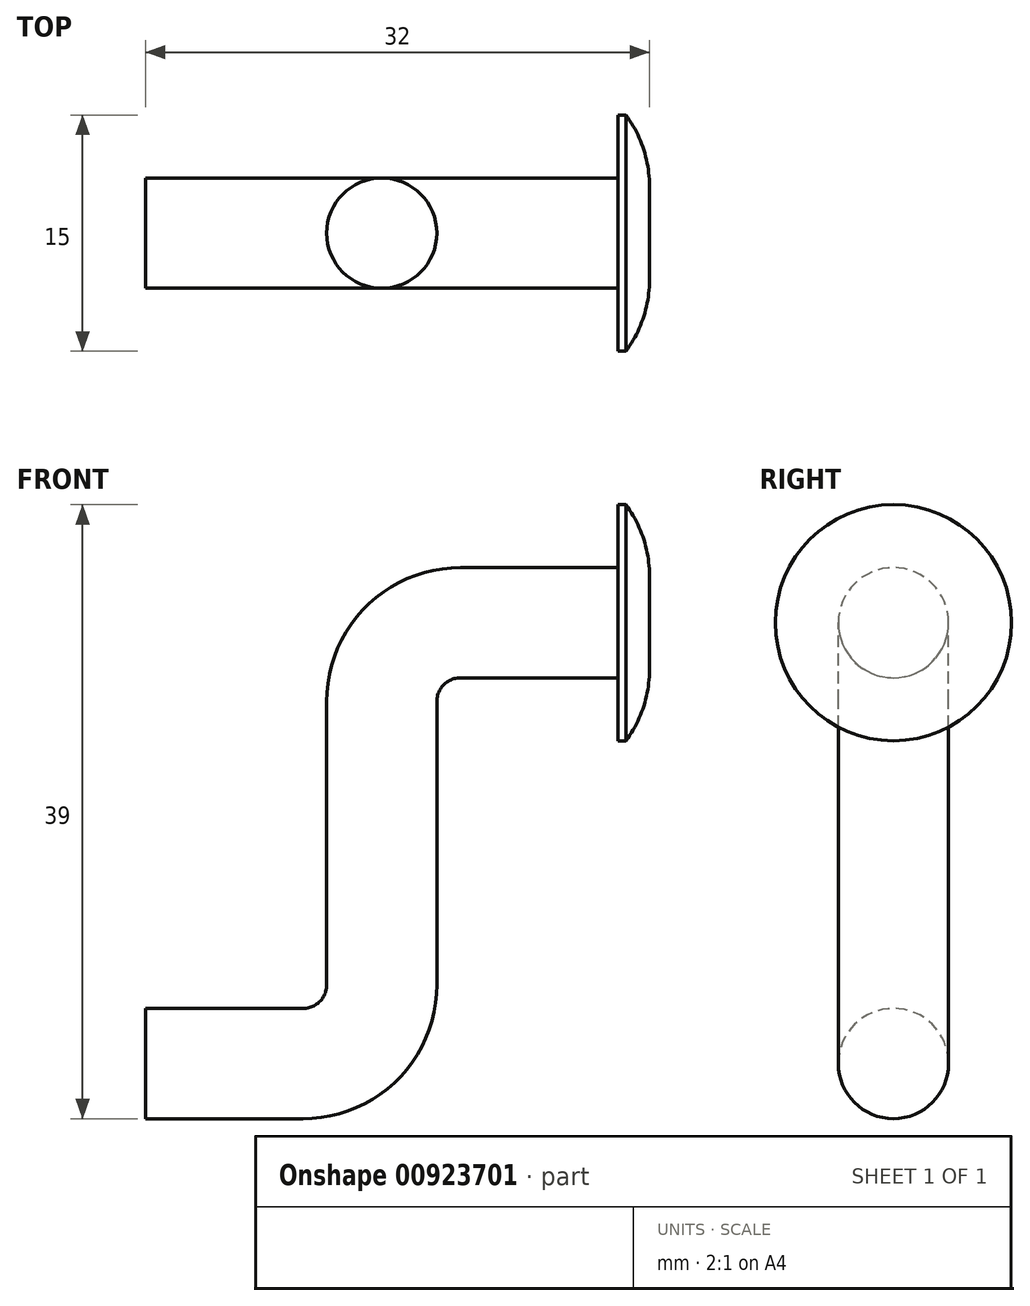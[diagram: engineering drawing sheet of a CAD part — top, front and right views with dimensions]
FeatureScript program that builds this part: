
annotation { "Feature Type Name" : "Feature", "Feature Type Description" : "" }
export const myFeature = defineFeature(function(context is Context, id is Id, definition is map)
    precondition{}
    {
        {
            var Q0;
            Q0=qCreatedBy(makeId("Front.planeOp"),FACE);
            var sketch = newSketch(context, id + "F0", { "sketchPlane" : qUnion([Q0])});
            skLineSegment(sketch, "E0", {"start": v(0, 0) * mm, "end": v(10, 0) * mm});
            skLineSegment(sketch, "E1", {"start": v(15, 5) * mm, "end": v(15, 23) * mm});
            skLineSegment(sketch, "E2", {"start": v(20, 28) * mm, "end": v(30, 28) * mm});
            skPoint(sketch, "E3.visualSharp", {"position": v(15, 0) * mm});
            skArc(sketch, "E3.filletArc", {"start": v(10, 0) * mm, "mid": v(13.54, 1.46) * mm, "end": v(15, 5) * mm});
            skPoint(sketch, "E4.visualSharp", {"position": v(15, 28) * mm});
            skArc(sketch, "E4.filletArc", {"start": v(20, 28) * mm, "mid": v(16.46, 26.54) * mm, "end": v(15, 23) * mm});
            skSolve(sketch);
        }
        {
            var Q0;
            Q0=qCreatedBy(makeId("Right.planeOp"),FACE);
            var sketch = newSketch(context, id + "F1", { "sketchPlane" : qUnion([Q0])});
            skCircle(sketch, "E5", {"center": v(0, 0) * mm, "radius": 3.5 * mm});
            skSolve(sketch);
        }
        {
            var Q0;
            Q0=makeQuery(id+"F1.imprint","IMPRINT",FACE,{"disambiguationData":[TD([[makeQuery(id+"F1.imprint","IMPRINT",EDGE,{"derivedFrom":sQuery(id+"F1.wireOp",EDGE,"E5")}),1.0]])]});
            var Q1;
            Q1=sQuery(id+"F0.wireOp",EDGE,"E0");
            var Q2;
            Q2=sQuery(id+"F0.wireOp",EDGE,"E3.filletArc");
            var Q3;
            Q3=sQuery(id+"F0.wireOp",EDGE,"E1");
            var Q4;
            Q4=sQuery(id+"F0.wireOp",EDGE,"E4.filletArc");
            var Q5;
            Q5=sQuery(id+"F0.wireOp",EDGE,"E2");
            sweep(context, id + "F2", {"profiles" : qUnion([Q0]), "path" : qUnion([Q1, Q2, Q3, Q4, Q5])});
        }
        {
            var Q0;
            Q0=makeQuery(id+"F2.opSweep","CAP_FACE",FACE,{"disambiguationData":[OSD([sQuery(id+"F0.wireOp",VERTEX,"E2.end"),sQuery(id+"F1.wireOp",EDGE,"E5")])],"isStart":false});
            var sketch = newSketch(context, id + "F3", { "sketchPlane" : qUnion([Q0])});
            skCircle(sketch, "E6", {"center": v(0, 28) * mm, "radius": 7.5 * mm});
            skSolve(sketch);
        }
        {
            var Q0;
            Q0=makeQuery(id+"F3.imprint","IMPRINT",FACE,{"disambiguationData":[TD([[makeQuery(id+"F3.imprint","IMPRINT",EDGE,{"derivedFrom":sQuery(id+"F3.wireOp",EDGE,"E6")}),1.0]])]});
            extrude(context, id + "F4", {"entities" : qUnion([Q0]), "depth" : 0.5 * mm, "offsetDistance" : 25 * mm});
        }
        {
            var Q0;
            Q0=makeQuery(id+"F2.opSweep","CAP_FACE",FACE,{"disambiguationData":[OSD([sQuery(id+"F0.wireOp",VERTEX,"E2.end"),sQuery(id+"F1.wireOp",EDGE,"E5")])],"isStart":false});
            extrude(context, id + "F5", {"entities" : qUnion([Q0]), "operationType" : NewBodyOperationType.ADD, "depth" : 0.5 * mm, "offsetDistance" : 25 * mm});
        }
        {
            var Q0;
            Q0=makeQuery(id+"F4.opExtrude","CAP_FACE",FACE,{"disambiguationData":[OSD([sQuery(id+"F0.wireOp",VERTEX,"E2.end"),sQuery(id+"F1.wireOp",EDGE,"E5"),sQuery(id+"F3.wireOp",EDGE,"E6")])],"isStart":false});
            var Q1;
            Q1=makeQuery(id+"F5.opExtrude","CAP_FACE",FACE,{"disambiguationData":[OSD([sQuery(id+"F0.wireOp",VERTEX,"E2.end"),sQuery(id+"F1.wireOp",EDGE,"E5")])],"isStart":false});
            extrude(context, id + "F6", {"entities" : qUnion([Q0, Q1]), "depth" : 1.5 * mm, "offsetDistance" : 25 * mm});
        }
        {
            var Q0;
            Q0=makeQuery(id+"F6.opExtrude","CAP_EDGE",EDGE,{"disambiguationData":[OSD([sQuery(id+"F3.wireOp",EDGE,"E6")])],"isStart":false});
            fillet(context, id + "F7", {"entities" : qUnion([Q0]), "tangentPropagation" : true, "radius" : 7.5 * mm, "defaultsChanged" : true, "vertexSettings" : [], "allowEdgeOverflow" : false});
        }
    });
